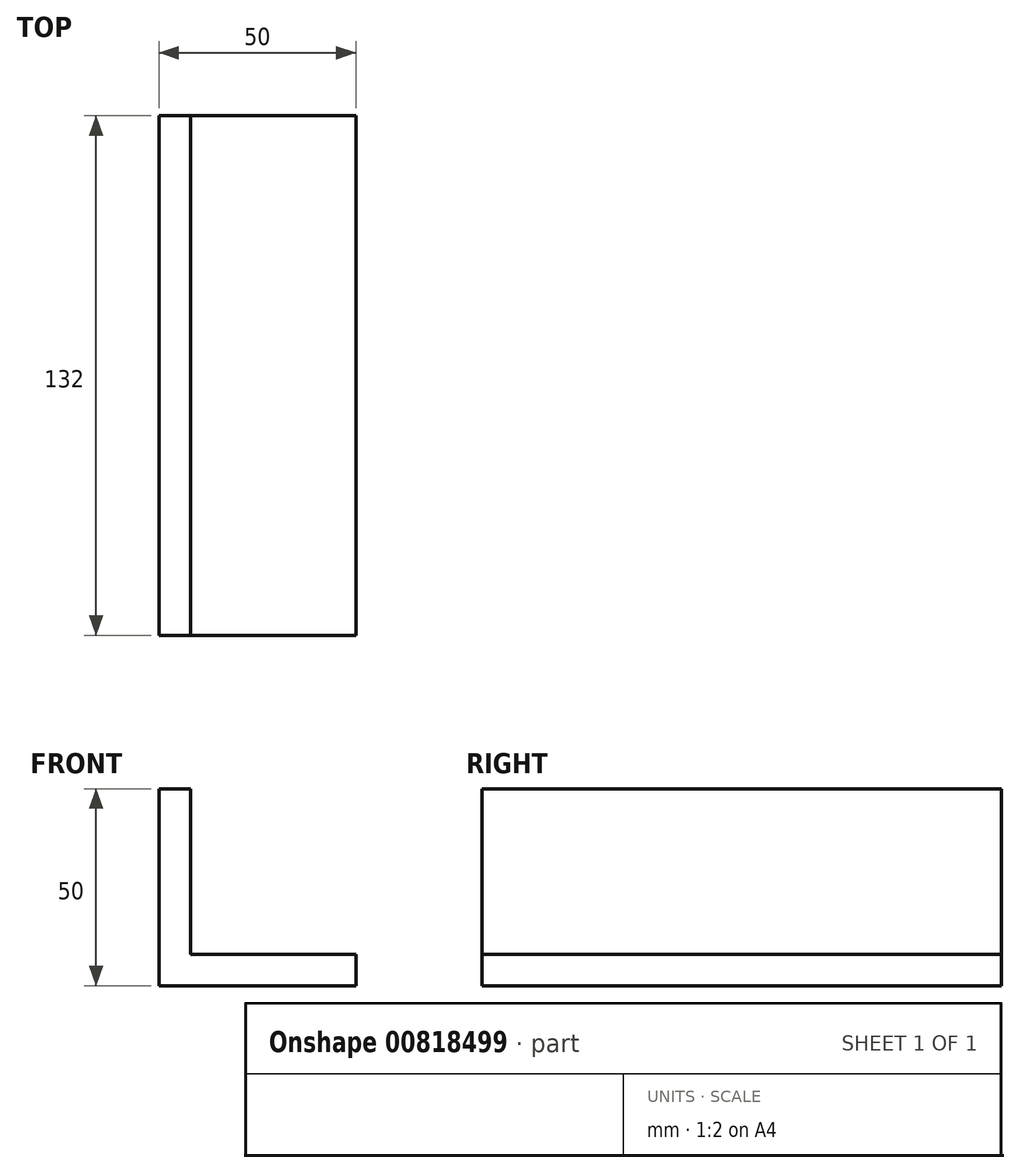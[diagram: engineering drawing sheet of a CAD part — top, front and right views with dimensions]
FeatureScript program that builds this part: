
annotation { "Feature Type Name" : "Feature", "Feature Type Description" : "" }
export const myFeature = defineFeature(function(context is Context, id is Id, definition is map)
    precondition{}
    {
        {
            var Q0;
            Q0=qCreatedBy(makeId("Front.planeOp"),FACE);
            var sketch = newSketch(context, id + "F0", { "sketchPlane" : qUnion([Q0])});
            skLineSegment(sketch, "E0.bottom", {"start": v(0, 0) * mm, "end": v(50, 0) * mm});
            skLineSegment(sketch, "E0.top", {"start": v(0, 50) * mm, "end": v(8, 50) * mm});
            skLineSegment(sketch, "E0.left", {"start": v(0, 0) * mm, "end": v(0, 50) * mm});
            skLineSegment(sketch, "E0.right", {"start": v(50, 0) * mm, "end": v(50, 8) * mm});
            skLineSegment(sketch, "E1.top", {"start": v(50, 8) * mm, "end": v(8, 8) * mm});
            skLineSegment(sketch, "E1.right", {"start": v(8, 50) * mm, "end": v(8, 8) * mm});
            skSolve(sketch);
        }
        {
            var Q0;
            Q0=qSketchRegion(id+"F0",true);
            extrude(context, id + "F1", {"entities" : qUnion([Q0]), "endBound" : BoundingType.SYMMETRIC, "depth" : 132 * mm});
        }
    });
